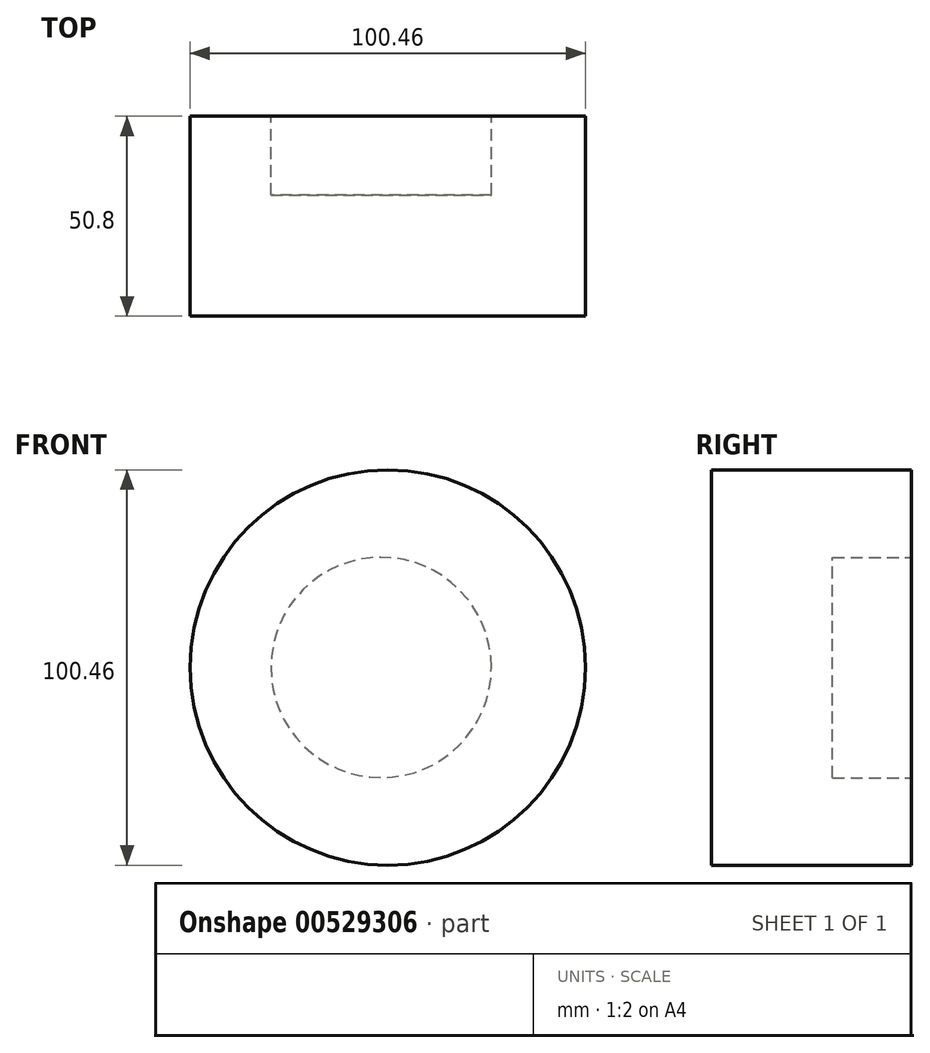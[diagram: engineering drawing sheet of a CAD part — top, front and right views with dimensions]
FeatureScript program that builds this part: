
annotation { "Feature Type Name" : "Feature", "Feature Type Description" : "" }
export const myFeature = defineFeature(function(context is Context, id is Id, definition is map)
    precondition{}
    {
        {
            var Q0;
            Q0=qCreatedBy(makeId("Front.planeOp"),FACE);
            var sketch = newSketch(context, id + "F0", { "sketchPlane" : qUnion([Q0])});
            skCircle(sketch, "E0", {"center": v(0, 0) * mm, "radius": 50.23 * mm});
            skSolve(sketch);
        }
        {
            var Q0;
            Q0=makeQuery(id+"F0.imprint","IMPRINT",FACE,{"disambiguationData":[TD([[makeQuery(id+"F0.imprint","IMPRINT",EDGE,{"derivedFrom":sQuery(id+"F0.wireOp",EDGE,"E0")}),1.0]])]});
            extrude(context, id + "F1", {"entities" : qUnion([Q0]), "depth" : 50.8 * mm, "offsetDistance" : 25.4 * mm});
        }
        {
            var Q0;
            Q0=qCreatedBy(makeId("Front.planeOp"),FACE);
            var sketch = newSketch(context, id + "F2", { "sketchPlane" : qUnion([Q0])});
            skLineSegment(sketch, "E1", {"start": v(0, 0) * mm, "end": v(0, -27.95) * mm});
            skCircle(sketch, "E2", {"center": v(-1.68, 0) * mm, "radius": 28 * mm});
            skSolve(sketch);
        }
        {
            var Q0;
            Q0=makeQuery(id+"F2.imprint","IMPRINT",FACE,{"disambiguationData":[TD([[makeQuery(id+"F2.imprint","IMPRINT",EDGE,{"derivedFrom":sQuery(id+"F2.wireOp",EDGE,"E2")}),1.0]])]});
            extrude(context, id + "F3", {"entities" : qUnion([Q0]), "oppositeDirection" : true, "depth" : -20 * mm, "offsetDistance" : 25 * mm});
        }
    });
